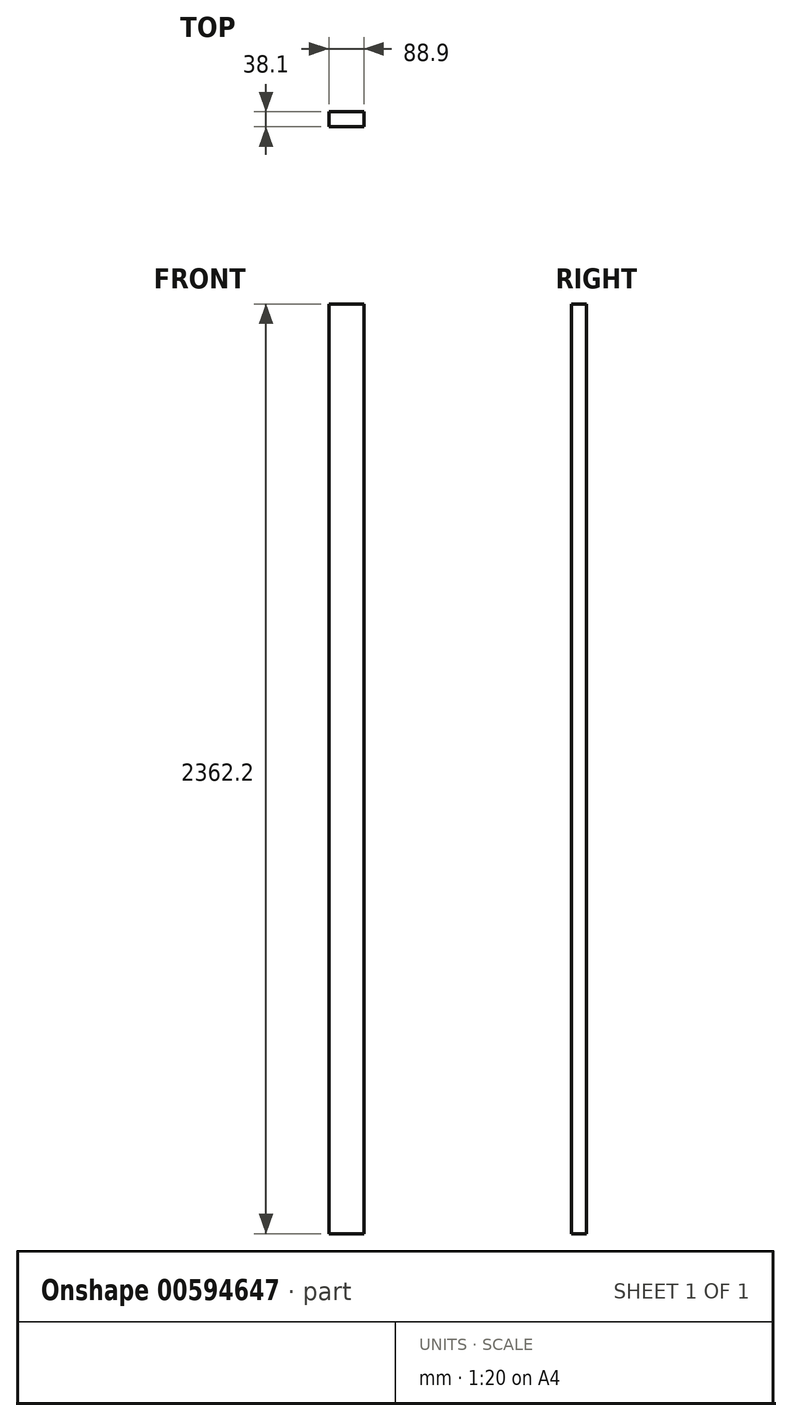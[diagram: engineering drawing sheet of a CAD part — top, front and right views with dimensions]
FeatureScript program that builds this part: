
annotation { "Feature Type Name" : "Feature", "Feature Type Description" : "" }
export const myFeature = defineFeature(function(context is Context, id is Id, definition is map)
    precondition{}
    {
        {
            var Q0;
            Q0=qCreatedBy(makeId("Front.planeOp"),FACE);
            var sketch = newSketch(context, id + "F0", { "sketchPlane" : qUnion([Q0])});
            skLineSegment(sketch, "E0.bottom", {"start": v(-44.45, -1181.1) * mm, "end": v(44.45, -1181.1) * mm});
            skLineSegment(sketch, "E0.top", {"start": v(-44.45, 1181.1) * mm, "end": v(44.45, 1181.1) * mm});
            skLineSegment(sketch, "E0.left", {"start": v(-44.45, -1181.1) * mm, "end": v(-44.45, 1181.1) * mm});
            skLineSegment(sketch, "E0.right", {"start": v(44.45, -1181.1) * mm, "end": v(44.45, 1181.1) * mm});
            skPoint(sketch, "E0.middle", {"position": v(0, 0) * mm});
            skSolve(sketch);
        }
        {
            var Q0;
            Q0=makeQuery(id+"F0.imprint","IMPRINT",FACE,{"disambiguationData":[TD([[makeQuery(id+"F0.imprint","IMPRINT",EDGE,{"derivedFrom":sQuery(id+"F0.wireOp",EDGE,"E0.bottom")}),1.0]])]});
            extrude(context, id + "F1", {"entities" : qUnion([Q0]), "endBound" : BoundingType.SYMMETRIC, "depth" : 38.1 * mm, "offsetDistance" : 25.4 * mm});
        }
    });
